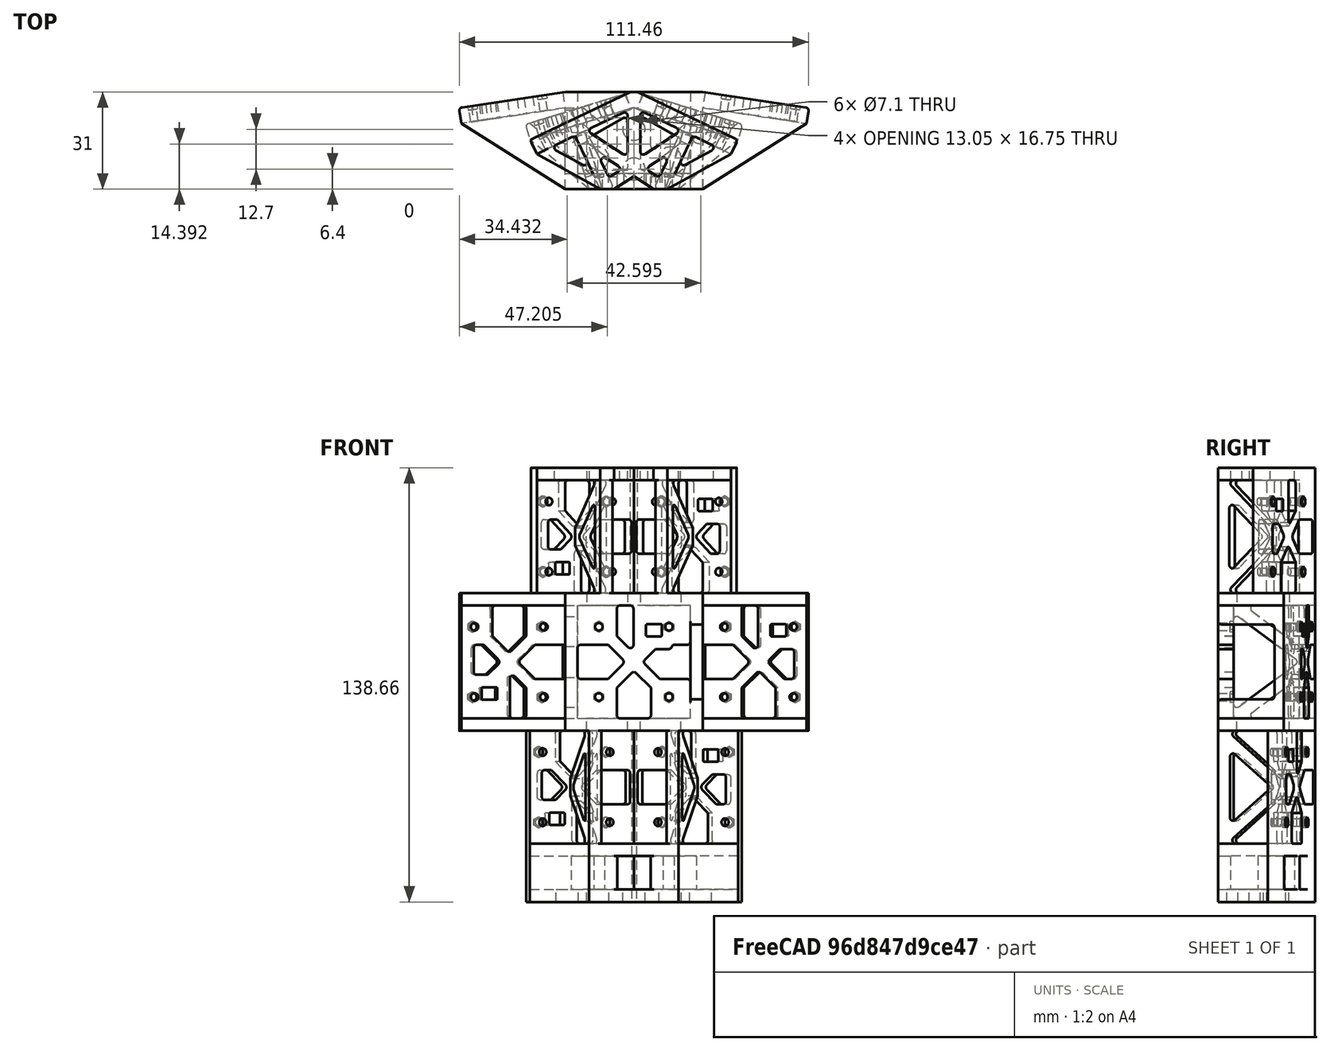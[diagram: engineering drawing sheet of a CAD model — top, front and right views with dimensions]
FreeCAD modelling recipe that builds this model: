
FCSTD DOCUMENT  (FreeCAD 0.20R)
Label: camAssembly
License: All rights reserved
LicenseURL: http://en.wikipedia.org/wiki/All_rights_reserved
objects: App::Link×10, App::DocumentObjectGroup×3, Part::Fillet×3, PartDesign::CoordinateSystem×1, App::FeaturePython×1, Spreadsheet::Sheet×1, App::Part×1, Part::MultiFuse×1, Part::Refine×1
note: 6 computed B-rep shape members (.brp) not serialized (recipe doc carries the construction recipe, not evaluated geometry)
EXTERNAL_REF file=topRowRack.FCStd obj=rowLCS
EXTERNAL_REF file=topRowRack.FCStd obj=Body
EXTERNAL_REF file=botRowRack.FCStd obj=rowLCS
EXTERNAL_REF file=botRowRack.FCStd obj=Body
EXTERNAL_REF file=midRowRack.FCStd obj=midRackLCS
EXTERNAL_REF file=midRowRack.FCStd obj=Body
EXTERNAL_REF file=centerMountPlate.FCStd obj=mountPlateLCS
EXTERNAL_REF file=midRowRack.FCStd obj=centerPlateLCS
EXTERNAL_REF file=centerMountPlate.FCStd obj=Body
EXTERNAL_REF file=midRowRack.FCStd obj=sidePlate1LCS
EXTERNAL_REF file=sideMountPlate.FCStd obj=mountPlateLCS
EXTERNAL_REF file=sideMountPlate.FCStd obj=Body
EXTERNAL_REF file=midRowRack.FCStd obj=sidePlate2LCS
EXTERNAL_REF file=cornerMountPlate.FCStd obj=mountPlateLCS
EXTERNAL_REF file=topRowRack.FCStd obj=plateLCS1
EXTERNAL_REF file=cornerMountPlate.FCStd obj=Body
EXTERNAL_REF file=topRowRack.FCStd obj=plateLCS2
EXTERNAL_REF file=botRowRack.FCStd obj=plateLCS1
EXTERNAL_REF file=botRowRack.FCStd obj=plateLCS2

FEATURE [App::DocumentObjectGroup] Parts
FEATURE [PartDesign::CoordinateSystem] LCS_Origin
  AttacherType = Attacher::AttachEngine3D
  MapMode = 2
  Support = -> [X_Axis]
FEATURE [App::DocumentObjectGroup] Constraints
FEATURE [App::FeaturePython] Variables  # WARN: FeaturePython — macro-defined, semantics opaque (R4)
  Type = App::PropertyContainer
FEATURE [App::DocumentObjectGroup] Configurations
FEATURE [App::Link] dualCamRow  label="topRowRack"
  AssemblyType = Part::Link
  AttachedBy = #rowLCS
  AttachedTo = Parent Assembly#LCS_Origin
  AttachmentOffset = pos=(0,0,40) rot=(0,0,1;0rad)
  ElementCount = 0
  LinkClaimChild = false
  LinkCopyOnChange = 0
  LinkCopyOnChangeTouched = false
  LinkPlacement = pos=(0,0,40) rot=(0,0,1;0rad)
  LinkTransform = false
  Placement = pos=(0,0,40) rot=(0,0,1;0rad)
  Scale = 1
  ScaleVector = (1,1,1)
  ShowElement = true
  SolverId = Asm4EE
  _LinkOwner = 0
  expr: .AttachmentOffset.Base.z = <<props>>.cellDiam
  expr: Placement = LCS_Origin.Placement * AttachmentOffset * topRowRack#rowLCS.Placement ^ -1
FEATURE [Spreadsheet::Sheet] Spreadsheet  label="props"
  cells = A2=cell diameter; B2=mm; C2(cellDiam)=40
FEATURE [App::Link] dualCamRow001  label="botRowRack"
  AssemblyType = Part::Link
  AttachedBy = #rowLCS
  AttachedTo = Parent Assembly#LCS_Origin
  AttachmentOffset = pos=(0,0,-40) rot=(0,1,0;3.14159rad)
  ElementCount = 0
  LinkClaimChild = false
  LinkCopyOnChange = 0
  LinkCopyOnChangeTouched = false
  LinkPlacement = pos=(0,0,-40) rot=(0,1,0;3.14159rad)
  LinkTransform = false
  Placement = pos=(0,0,-40) rot=(0,1,0;3.14159rad)
  Scale = 1
  ScaleVector = (1,1,1)
  ShowElement = true
  SolverId = Asm4EE
  _LinkOwner = 0
  expr: .AttachmentOffset.Base.z = -<<props>>.cellDiam
  expr: Placement = LCS_Origin.Placement * AttachmentOffset * botRowRack#rowLCS.Placement ^ -1
FEATURE [App::Link] midRowRack
  AssemblyType = Part::Link
  AttachedBy = #midRackLCS
  AttachedTo = Parent Assembly#LCS_Origin
  ElementCount = 0
  LinkClaimChild = false
  LinkCopyOnChange = 0
  LinkCopyOnChangeTouched = false
  LinkTransform = false
  Scale = 1
  ScaleVector = (1,1,1)
  ShowElement = true
  SolverId = Asm4EE
  _LinkOwner = 0
  expr: Placement = LCS_Origin.Placement * AttachmentOffset * midRowRack#midRackLCS.Placement ^ -1
FEATURE [App::Link] mountPlate  label="centerPlate"
  AssemblyType = Part::Link
  AttachedBy = #mountPlateLCS
  AttachedTo = midRowRack#centerPlateLCS
  ElementCount = 0
  LinkClaimChild = false
  LinkCopyOnChange = 0
  LinkCopyOnChangeTouched = false
  LinkPlacement = pos=(0,-26,0) rot=(0,0,1;0rad)
  LinkTransform = false
  Placement = pos=(0,-26,0) rot=(0,0,1;0rad)
  Scale = 1
  ScaleVector = (1,1,1)
  ShowElement = true
  SolverId = Asm4EE
  _LinkOwner = 0
  expr: Placement = midRowRack.Placement * midRowRack#centerPlateLCS.Placement * AttachmentOffset * centerMountPlate#mountPlateLCS.Placement ^ -1
FEATURE [App::Link] mountPlate001  label="sidePlate1"
  AssemblyType = Part::Link
  AttachedBy = #mountPlateLCS
  AttachedTo = midRowRack#sidePlate1LCS
  ElementCount = 0
  LinkClaimChild = false
  LinkCopyOnChange = 0
  LinkCopyOnChangeTouched = false
  LinkPlacement = pos=(40.5413,-2.77102,-6e-16) rot=(0,0,-1;0.148353rad)
  LinkTransform = false
  Placement = pos=(40.5413,-2.77102,-6e-16) rot=(0,0,-1;0.148353rad)
  Scale = 1
  ScaleVector = (1,1,1)
  ShowElement = true
  SolverId = Asm4EE
  _LinkOwner = 0
  expr: Placement = midRowRack.Placement * midRowRack#sidePlate1LCS.Placement * AttachmentOffset * sideMountPlate#mountPlateLCS.Placement ^ -1
FEATURE [App::Link] mountPlate002  label="sidePlate2"
  AssemblyType = Part::Link
  AttachedBy = #mountPlateLCS
  AttachedTo = midRowRack#sidePlate2LCS
  ElementCount = 0
  LinkClaimChild = false
  LinkCopyOnChange = 0
  LinkCopyOnChangeTouched = false
  LinkPlacement = pos=(-40.5413,-2.77102,-7e-16) rot=(-0.074108,0.99725,0;3.14159rad)
  LinkTransform = false
  Placement = pos=(-40.5413,-2.77102,-7e-16) rot=(-0.074108,0.99725,0;3.14159rad)
  Scale = 1
  ScaleVector = (1,1,1)
  ShowElement = true
  SolverId = Asm4EE
  _LinkOwner = 0
  expr: Placement = midRowRack.Placement * midRowRack#sidePlate2LCS.Placement * AttachmentOffset * sideMountPlate#mountPlateLCS.Placement ^ -1
FEATURE [App::Link] mountPlate003  label="topPllate1"
  AssemblyType = Part::Link
  AttachedBy = #mountPlateLCS
  AttachedTo = dualCamRow#plateLCS1
  ElementCount = 0
  LinkClaimChild = false
  LinkCopyOnChange = 0
  LinkCopyOnChangeTouched = false
  LinkPlacement = pos=(19.1831,-8.61022,40) rot=(0,0,-1;0.445059rad)
  LinkTransform = false
  Placement = pos=(19.1831,-8.61022,40) rot=(0,0,-1;0.445059rad)
  Scale = 1
  ScaleVector = (1,1,1)
  ShowElement = true
  SolverId = Asm4EE
  _LinkOwner = 0
  expr: Placement = dualCamRow.Placement * topRowRack#plateLCS1.Placement * AttachmentOffset * cornerMountPlate#mountPlateLCS.Placement ^ -1
FEATURE [App::Link] mountPlate004  label="topPlate2"
  AssemblyType = Part::Link
  AttachedBy = #mountPlateLCS
  AttachedTo = dualCamRow#plateLCS2
  ElementCount = 0
  LinkClaimChild = false
  LinkCopyOnChange = 0
  LinkCopyOnChangeTouched = false
  LinkPlacement = pos=(-19.1831,-8.61022,40) rot=(-0.220697,0.975342,0;3.14159rad)
  LinkTransform = false
  Placement = pos=(-19.1831,-8.61022,40) rot=(-0.220697,0.975342,0;3.14159rad)
  Scale = 1
  ScaleVector = (1,1,1)
  ShowElement = true
  SolverId = Asm4EE
  _LinkOwner = 0
  expr: Placement = dualCamRow.Placement * topRowRack#plateLCS2.Placement * AttachmentOffset * cornerMountPlate#mountPlateLCS.Placement ^ -1
FEATURE [App::Link] mountPlate005  label="botPlate1"
  AssemblyType = Part::Link
  AttachedBy = #mountPlateLCS
  AttachedTo = dualCamRow001#plateLCS1
  ElementCount = 0
  LinkClaimChild = false
  LinkCopyOnChange = 0
  LinkCopyOnChangeTouched = false
  LinkPlacement = pos=(-19.8734,-5.84743,-40) rot=(-0.147809,0.989016,0;3.14159rad)
  LinkTransform = false
  Placement = pos=(-19.8734,-5.84743,-40) rot=(-0.147809,0.989016,0;3.14159rad)
  Scale = 1
  ScaleVector = (1,1,1)
  ShowElement = true
  SolverId = Asm4EE
  _LinkOwner = 0
  expr: Placement = dualCamRow001.Placement * botRowRack#plateLCS1.Placement * AttachmentOffset * cornerMountPlate#mountPlateLCS.Placement ^ -1
FEATURE [App::Link] mountPlate006  label="botPlate2"
  AssemblyType = Part::Link
  AttachedBy = #mountPlateLCS
  AttachedTo = dualCamRow001#plateLCS2
  ElementCount = 0
  LinkClaimChild = false
  LinkCopyOnChange = 0
  LinkCopyOnChangeTouched = false
  LinkPlacement = pos=(19.8734,-5.84743,-40) rot=(0,0,1;5.98648rad)
  LinkTransform = false
  Placement = pos=(19.8734,-5.84743,-40) rot=(0,0,1;5.98648rad)
  Scale = 1
  ScaleVector = (1,1,1)
  ShowElement = true
  SolverId = Asm4EE
  _LinkOwner = 0
  expr: Placement = dualCamRow001.Placement * botRowRack#plateLCS2.Placement * AttachmentOffset * cornerMountPlate#mountPlateLCS.Placement ^ -1
FEATURE [App::Part] Model
  AssemblyType = Part::Link
  Group = -> [LCS_Origin,Constraints,Variables,Configurations,dualCamRow,dualCamRow001,midRowRack,mountPlate,mountPlate001,mountPlate002,mountPlate003,mountPlate004,mountPlate005,mountPlate006]
  Origin = -> Origin
  Type = Assembly
FEATURE [Part::MultiFuse] Fusion  label="fused"
  Refine = false
  Shapes = -> [dualCamRow,dualCamRow001,midRowRack,mountPlate,mountPlate001,mountPlate002,mountPlate003,mountPlate004,mountPlate005,mountPlate006]
FEATURE [Part::Refine] Fusion001  label="refined"
  Source = -> Fusion
FEATURE [Part::Fillet] Fillet  label="plateFillet"
  Base = -> Fusion001
FEATURE [Part::Fillet] Fillet001  label="ribFillet"
  Base = -> Fillet
FEATURE [Part::Fillet] Fillet002  label="edgeFillet"
  Base = -> Fillet001
